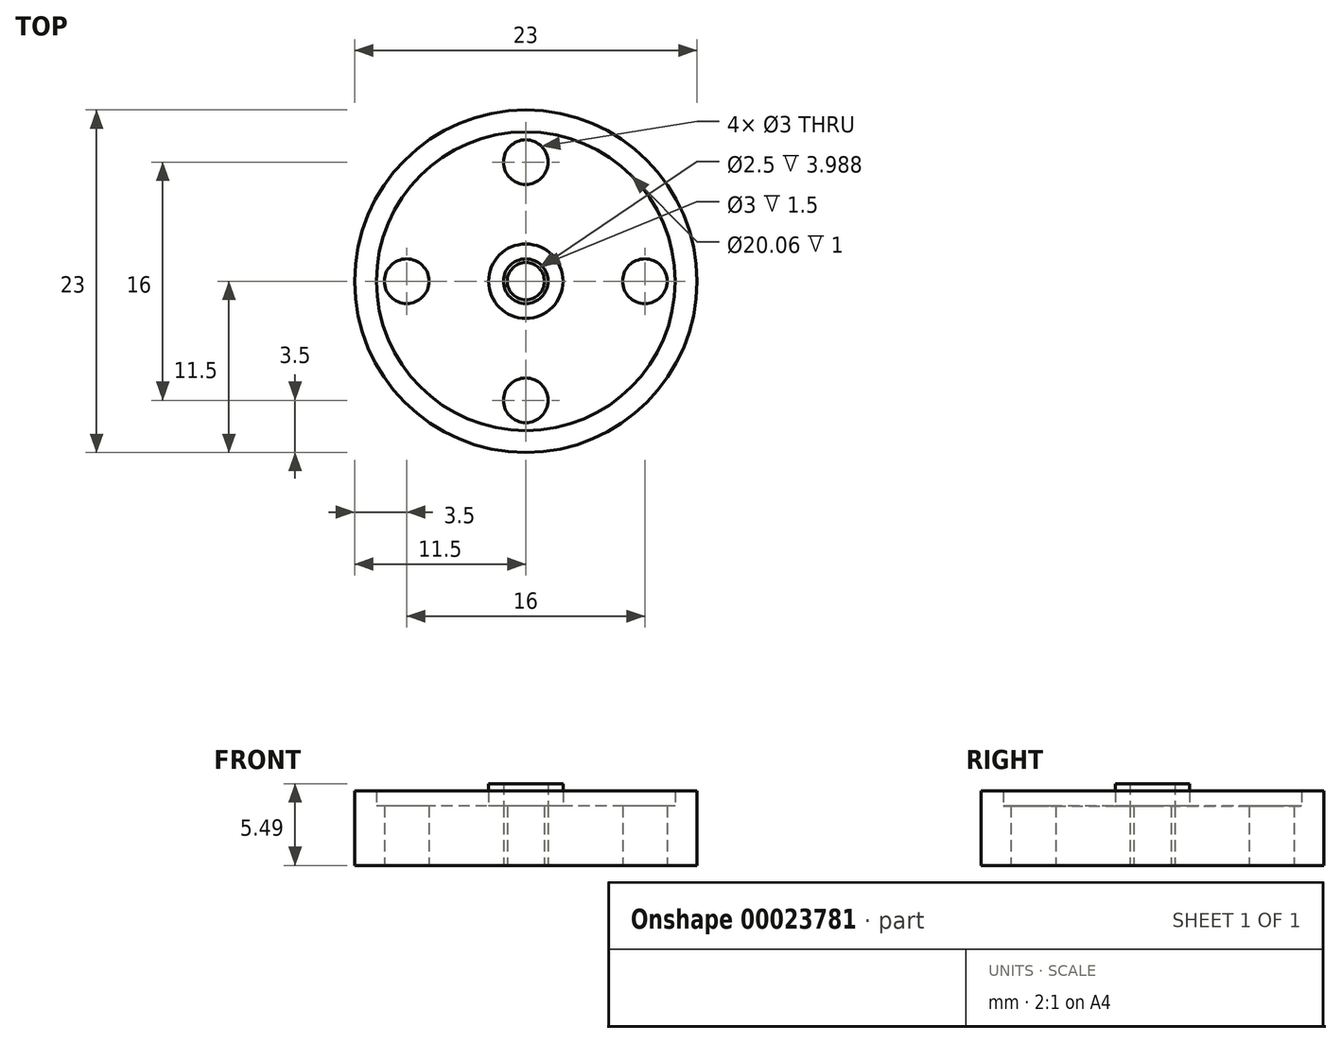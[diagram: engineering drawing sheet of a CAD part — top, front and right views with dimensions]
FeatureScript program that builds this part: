
annotation { "Feature Type Name" : "Feature", "Feature Type Description" : "" }
export const myFeature = defineFeature(function(context is Context, id is Id, definition is map)
    precondition{}
    {
        {
            var Q0;
            Q0=qCreatedBy(makeId("Top.planeOp"),FACE);
            var sketch = newSketch(context, id + "F0", { "sketchPlane" : qUnion([Q0])});
            skCircle(sketch, "E0", {"center": v(0, 0) * mm, "radius": 11.5 * mm});
            skCircle(sketch, "E1", {"center": v(0, 0) * mm, "radius": 1.25 * mm});
            skCircle(sketch, "E2", {"center": v(0, 0) * mm, "radius": 2 * mm});
            skCircle(sketch, "E3", {"center": v(0, 8) * mm, "radius": 1.5 * mm});
            skCircle(sketch, "E4.1.0", {"center": v(-8, 0) * mm, "radius": 1.5 * mm});
            skCircle(sketch, "E4.2.0", {"center": v(0, -8) * mm, "radius": 1.5 * mm});
            skCircle(sketch, "E4.3.0", {"center": v(8, 0) * mm, "radius": 1.5 * mm});
            skSolve(sketch);
        }
        {
            var Q0;
            Q0=makeQuery(id+"F0.imprint","IMPRINT",FACE,{"disambiguationData":[TD([[makeQuery(id+"F0.imprint","IMPRINT",EDGE,{"derivedFrom":sQuery(id+"F0.wireOp",EDGE,"E0")}),1.0]])]});
            var Q1;
            Q1=makeQuery(id+"F0.imprint","IMPRINT",FACE,{"disambiguationData":[TD([[makeQuery(id+"F0.imprint","IMPRINT",EDGE,{"derivedFrom":sQuery(id+"F0.wireOp",EDGE,"E1")}),-1.0]])]});
            extrude(context, id + "F1", {"entities" : qUnion([Q0, Q1]), "depth" : 4 * mm});
        }
        {
            var Q0;
            Q0=makeQuery(id+"F1.opExtrude","CAP_FACE",FACE,{"disambiguationData":[OSD([sQuery(id+"F0.wireOp",EDGE,"E0"),sQuery(id+"F0.wireOp",EDGE,"E2"),sQuery(id+"F0.wireOp",EDGE,"E3"),sQuery(id+"F0.wireOp",EDGE,"E4.1.0"),sQuery(id+"F0.wireOp",EDGE,"E4.2.0"),sQuery(id+"F0.wireOp",EDGE,"E4.3.0")])],"isStart":false});
            var sketch = newSketch(context, id + "F2", { "sketchPlane" : qUnion([Q0])});
            skCircle(sketch, "E5", {"center": v(0, 0) * mm, "radius": 1.5 * mm});
            skCircle(sketch, "E6", {"center": v(0, 0) * mm, "radius": 2.5 * mm});
            skCircle(sketch, "E7", {"center": v(0, 0) * mm, "radius": 10.06 * mm});
            skSolve(sketch);
        }
        {
            var Q0;
            Q0=makeQuery(id+"F2.imprint","IMPRINT",FACE,{"disambiguationData":[TD([[makeQuery(id+"F2.imprint","IMPRINT",EDGE,{"derivedFrom":sQuery(id+"F2.wireOp",EDGE,"E5")}),-1.0]])]});
            extrude(context, id + "F3", {"entities" : qUnion([Q0]), "operationType" : NewBodyOperationType.ADD, "depth" : 1.5 * mm});
        }
        {
            var Q0;
            {var subQ0=sQuery(id+"F0.wireOp",EDGE,"E0");var subQ1=sQuery(id+"F0.wireOp",EDGE,"E3");var subQ2=sQuery(id+"F0.wireOp",EDGE,"E4.1.0");var subQ3=sQuery(id+"F0.wireOp",EDGE,"E4.2.0");var subQ4=sQuery(id+"F0.wireOp",EDGE,"E4.3.0");Q0=makeQuery(id+"F3.boolean.opBoolean","SPLIT",FACE,{"disambiguationData":[TD([makeQuery(id+"F1.opExtrude","SWEPT_FACE",FACE,{"disambiguationData":[OSD([subQ0])]})])],"derivedFrom":makeQuery(id+"F1.opExtrude","CAP_FACE",FACE,{"disambiguationData":[OSD([subQ0,sQuery(id+"F0.wireOp",EDGE,"E1"),subQ1,subQ2,subQ3,subQ4])],"isStart":false})});}
            var sketch = newSketch(context, id + "F4", { "sketchPlane" : qUnion([Q0])});
            skCircle(sketch, "E8", {"center": v(0, 0) * mm, "radius": 10.03 * mm});
            skSolve(sketch);
        }
        {
            var Q0;
            Q0=makeQuery(id+"F4.imprint","IMPRINT",FACE,{"disambiguationData":[TD([[makeQuery(id+"F4.imprint","IMPRINT",EDGE,{"derivedFrom":sQuery(id+"F4.wireOp",EDGE,"E8")}),-1.0]])]});
            extrude(context, id + "F5", {"entities" : qUnion([Q0]), "operationType" : NewBodyOperationType.ADD, "depth" : 1 * mm});
        }
    });
